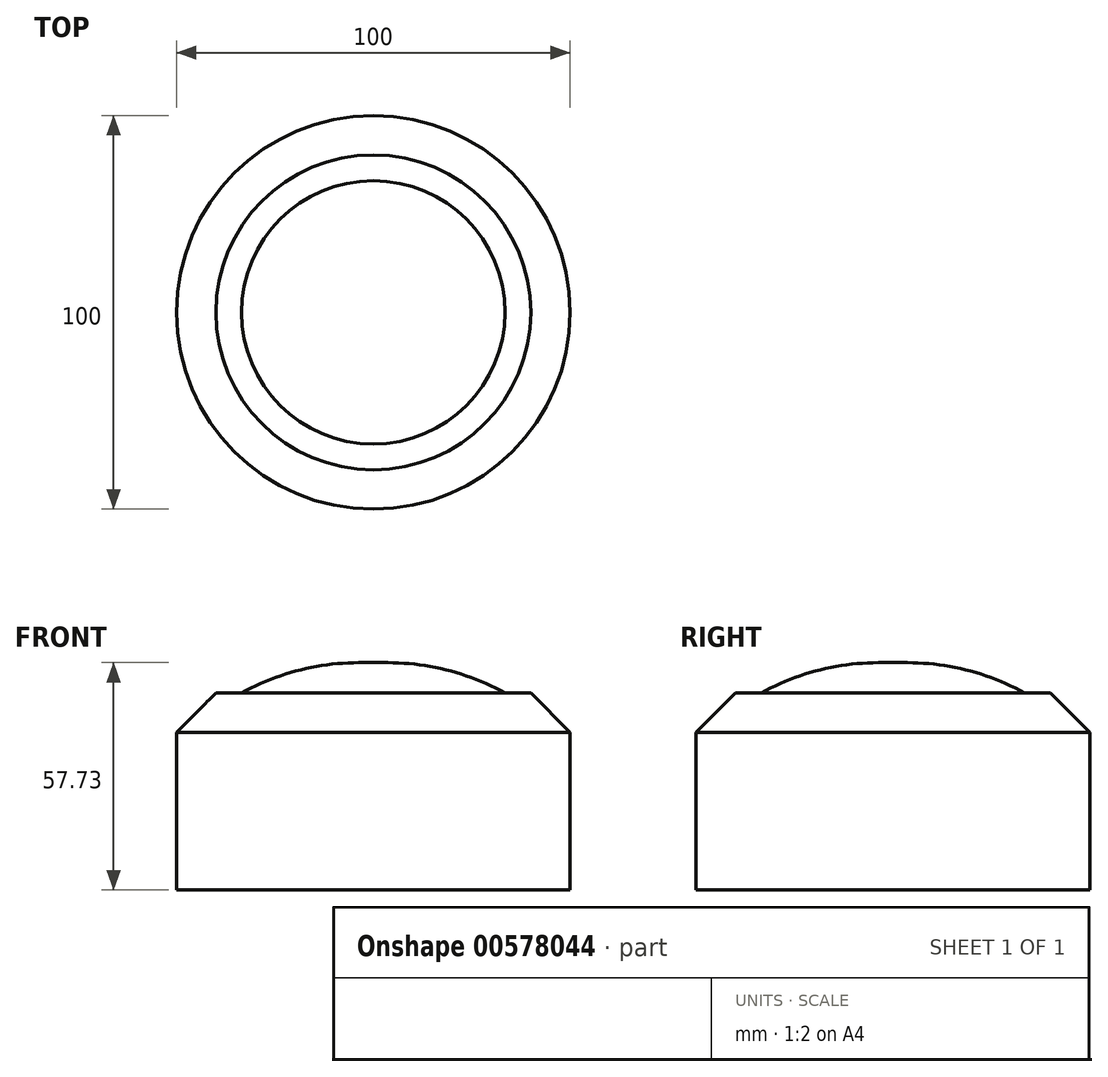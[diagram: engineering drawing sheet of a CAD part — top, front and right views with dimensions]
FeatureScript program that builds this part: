
annotation { "Feature Type Name" : "Feature", "Feature Type Description" : "" }
export const myFeature = defineFeature(function(context is Context, id is Id, definition is map)
    precondition{}
    {
        {
            var Q0;
            Q0=qCreatedBy(makeId("Front.planeOp"),FACE);
            var sketch = newSketch(context, id + "F0", { "sketchPlane" : qUnion([Q0])});
            skLineSegment(sketch, "E0.bottom", {"start": v(0, 0) * mm, "end": v(-50, 0) * mm});
            skLineSegment(sketch, "E0.top", {"start": v(0, 50) * mm, "end": v(-50, 50) * mm});
            skLineSegment(sketch, "E0.left", {"start": v(0, 0) * mm, "end": v(0, 50) * mm});
            skLineSegment(sketch, "E0.right", {"start": v(-50, 0) * mm, "end": v(-50, 50) * mm});
            skSolve(sketch);
        }
        {
            var Q0;
            Q0 = qSketchRegion(id + "F0", true);
            var Q1;
            Q1=sQuery(id+"F0.wireOp",EDGE,"E0.left");
            revolve(context, id + "F1", {"entities" : qUnion([Q0]), "axis" : qUnion([Q1]), "revolveType" : RevolveType.FULL});
        }
        {
            var Q0;
            Q0=qCreatedBy(makeId("Front.planeOp"),FACE);
            var sketch = newSketch(context, id + "F2", { "sketchPlane" : qUnion([Q0])});
            skLineSegment(sketch, "E1.bottom", {"start": v(0, 35.53) * mm, "end": v(-33.45, 35.53) * mm});
            skLineSegment(sketch, "E1.top", {"start": v(0, 57.73) * mm, "end": v(-33.45, 57.73) * mm});
            skLineSegment(sketch, "E1.left", {"start": v(0, 35.53) * mm, "end": v(0, 57.73) * mm});
            skLineSegment(sketch, "E1.right", {"start": v(-33.45, 35.53) * mm, "end": v(-33.45, 57.73) * mm});
            skSolve(sketch);
        }
        {
            var Q0;
            Q0 = qSketchRegion(id + "F2", true);
            var Q1;
            Q1=makeQuery(id+"F1.opRevolve","SWEPT_FACE",FACE,{"disambiguationData":[OSD([sQuery(id+"F0.wireOp",EDGE,"E0.right")])]});
            revolve(context, id + "F3", {"operationType" : NewBodyOperationType.ADD, "entities" : qUnion([Q0]), "axis" : qUnion([Q1]), "revolveType" : RevolveType.FULL});
        }
        {
            var Q0;
            Q0=makeQuery(id+"F3.opRevolve","SWEPT_EDGE",EDGE,{"disambiguationData":[OSD([sQuery(id+"F2.wireOp",EDGE,"E1.top"),sQuery(id+"F2.wireOp",EDGE,"E1.right")])]});
            fillet(context, id + "F4", {"entities" : qUnion([Q0]), "radius" : 61.08 * mm, "tangentPropagation" : true, "allowEdgeOverflow" : false});
        }
        {
            var Q0;
            Q0=makeQuery(id+"F1.opRevolve","SWEPT_EDGE",EDGE,{"disambiguationData":[OSD([sQuery(id+"F0.wireOp",EDGE,"E0.top"),sQuery(id+"F0.wireOp",EDGE,"E0.right")])]});
            chamfer(context, id + "F5", {"entities" : qUnion([Q0]), "width" : 10 * mm, "tangentPropagation" : true});
        }
    });
